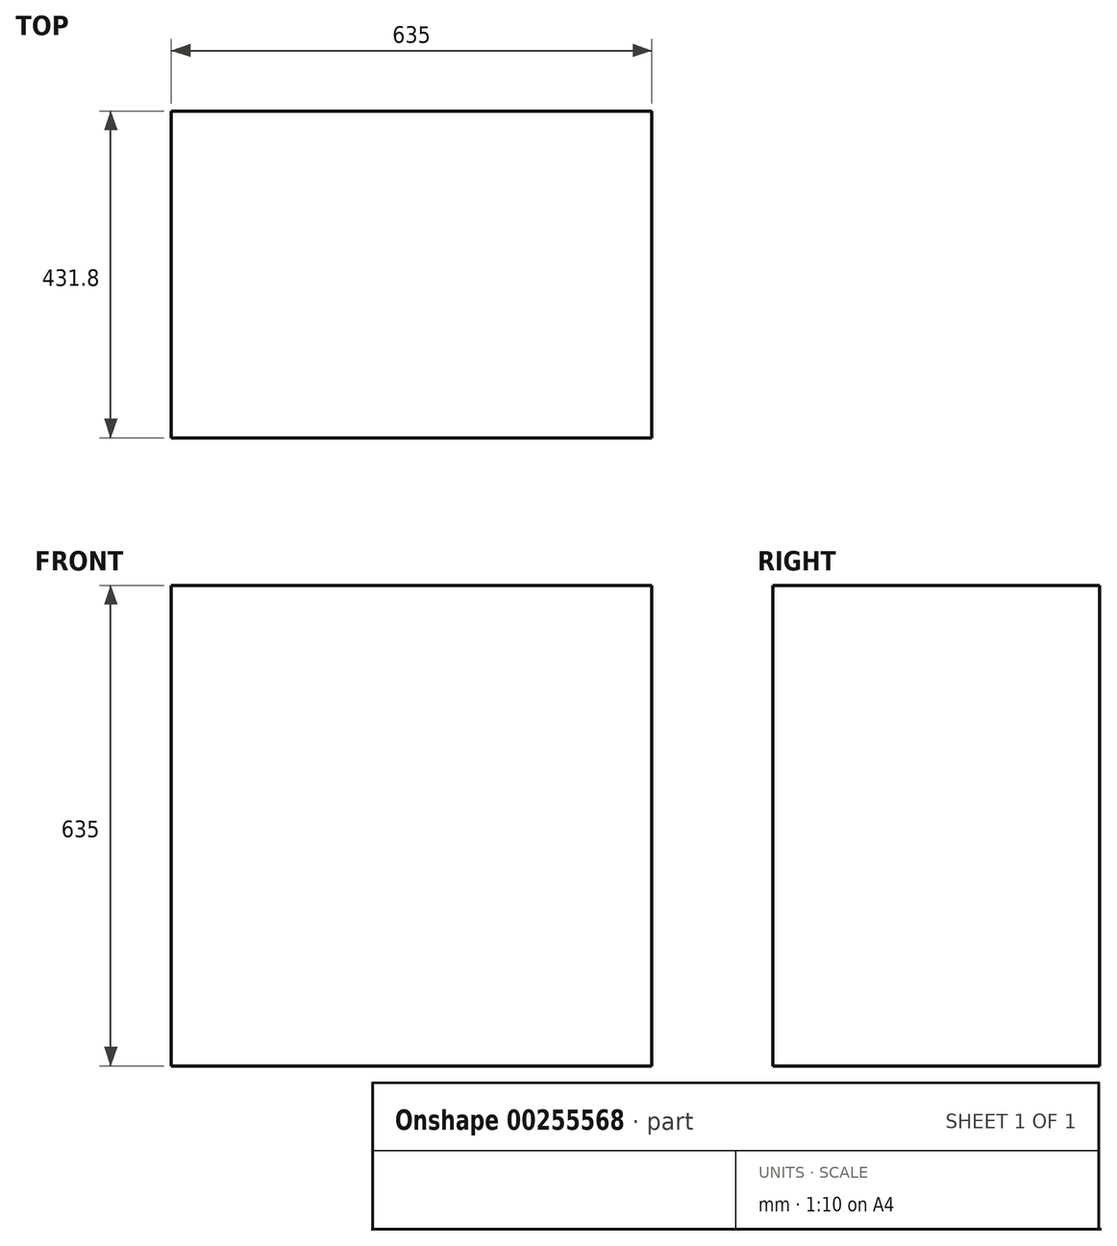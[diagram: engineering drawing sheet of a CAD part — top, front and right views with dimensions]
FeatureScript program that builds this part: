
annotation { "Feature Type Name" : "Feature", "Feature Type Description" : "" }
export const myFeature = defineFeature(function(context is Context, id is Id, definition is map)
    precondition{}
    {
        {
            var Q0;
            Q0=qCreatedBy(makeId("Front.planeOp"),FACE);
            var sketch = newSketch(context, id + "F0", { "sketchPlane" : qUnion([Q0])});
            skLineSegment(sketch, "E0.bottom", {"start": v(0, 0) * mm, "end": v(635, 0) * mm});
            skLineSegment(sketch, "E0.top", {"start": v(0, 635) * mm, "end": v(635, 635) * mm});
            skLineSegment(sketch, "E0.left", {"start": v(0, 0) * mm, "end": v(0, 635) * mm});
            skLineSegment(sketch, "E0.right", {"start": v(635, 0) * mm, "end": v(635, 635) * mm});
            skSolve(sketch);
        }
        {
            var Q0;
            Q0 = qSketchRegion(id + "F0", true);
            extrude(context, id + "F1", {"entities" : qUnion([Q0]), "depth" : 431.8 * mm});
        }
    });
